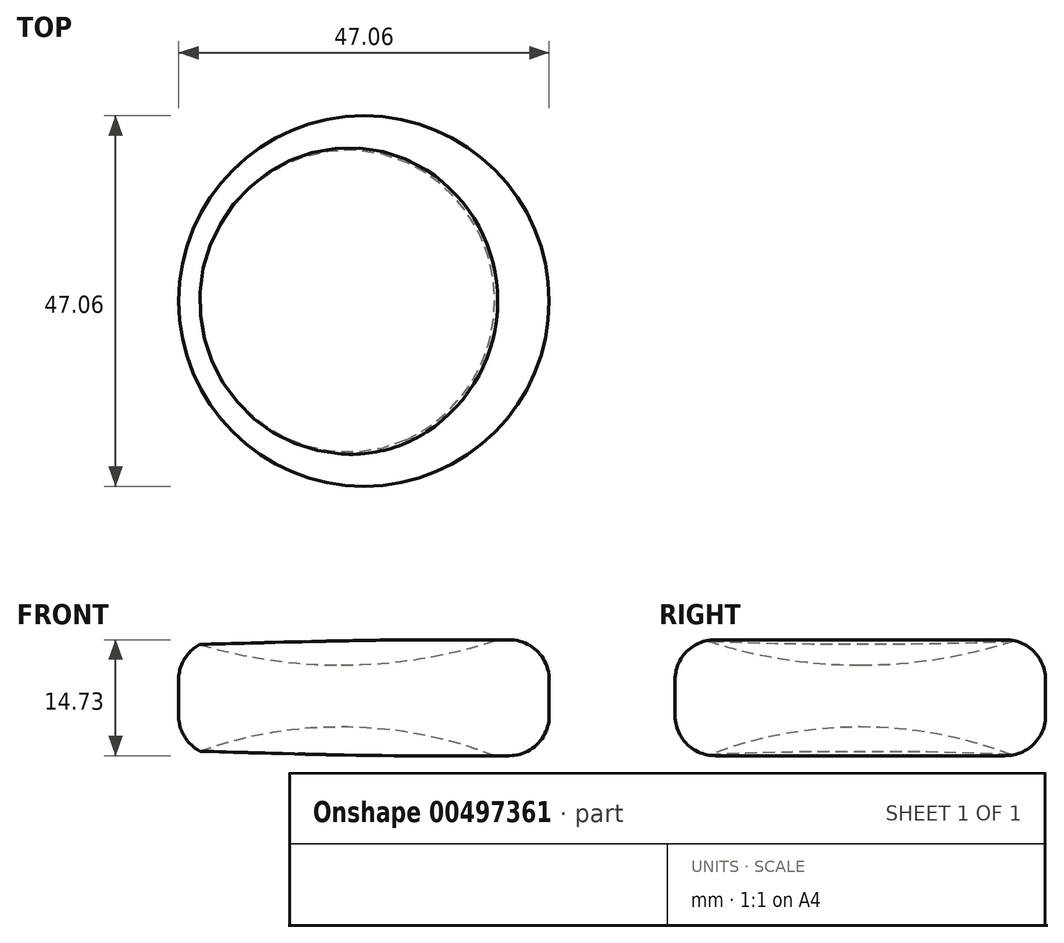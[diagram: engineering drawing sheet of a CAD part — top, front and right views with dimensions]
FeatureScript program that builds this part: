
annotation { "Feature Type Name" : "Feature", "Feature Type Description" : "" }
export const myFeature = defineFeature(function(context is Context, id is Id, definition is map)
    precondition{}
    {
        {
            var Q0;
            Q0=qCreatedBy(makeId("Top.planeOp"),FACE);
            var sketch = newSketch(context, id + "F0", { "sketchPlane" : qUnion([Q0])});
            skCircle(sketch, "E0", {"center": v(2.88, 0) * mm, "radius": 23.53 * mm});
            skSolve(sketch);
        }
        {
            var Q0;
            Q0=makeQuery(id+"F0.imprint","IMPRINT",FACE,{"disambiguationData":[TD([[makeQuery(id+"F0.imprint","IMPRINT",EDGE,{"derivedFrom":sQuery(id+"F0.wireOp",EDGE,"E0")}),1.0]])]});
            extrude(context, id + "F1", {"entities" : qUnion([Q0]), "depth" : 14.73 * mm});
        }
        {
            var Q0;
            Q0=makeQuery(id+"F1.opExtrude","SWEPT_FACE",FACE,{"disambiguationData":[OSD([sQuery(id+"F0.wireOp",EDGE,"E0")])]});
            fillet(context, id + "F2", {"entities" : qUnion([Q0]), "radius" : 5.08 * mm, "tangentPropagation" : true, "allowEdgeOverflow" : false});
        }
        {
            var Q0;
            Q0=qCreatedBy(makeId("Right.planeOp"),FACE);
            var sketch = newSketch(context, id + "F3", { "sketchPlane" : qUnion([Q0])});
            skCircle(sketch, "E1", {"center": v(0, -50.28) * mm, "radius": 53.92 * mm});
            skLineSegment(sketch, "E2", {"start": v(0, -50.28) * mm, "end": v(-53.92, -50.28) * mm});
            skLineSegment(sketch, "E3", {"start": v(-53.92, -50.28) * mm, "end": v(53.92, -50.28) * mm});
            skSolve(sketch);
        }
        {
            var Q0;
            {var subQ0=sQuery(id+"F3.wireOp",EDGE,"E3");var subQ4=makeQuery(id+"F3.imprint","IMPRINT",VERTEX,{"derivedFrom":subQ0});Q0=makeQuery(id+"F3.imprint","IMPRINT",FACE,{"disambiguationData":[TD([[makeQuery(id+"F3.imprint","IMPRINT",EDGE,{"disambiguationData":[TD([[subQ4,1.0]])],"derivedFrom":subQ0}),1.0]])]});}
            var Q1;
            Q1=sQuery(id+"F3.wireOp",EDGE,"E3");
            revolve(context, id + "F4", {"operationType" : NewBodyOperationType.REMOVE, "entities" : qUnion([Q0]), "axis" : qUnion([Q1]), "revolveType" : RevolveType.FULL, "oppositeDirection" : true});
        }
        {
            var Q0;
            Q0=qCreatedBy(makeId("Front.planeOp"),FACE);
            var sketch = newSketch(context, id + "F5", { "sketchPlane" : qUnion([Q0])});
            skCircle(sketch, "E4", {"center": v(0, -75.78) * mm, "radius": 78.03 * mm});
            skLineSegment(sketch, "E5", {"start": v(0, -162.58) * mm, "end": v(0, 39.57) * mm});
            skSolve(sketch);
        }
        {
            var Q0;
            {var subQ0=sQuery(id+"F5.wireOp",EDGE,"E5");var subQ1=sQuery(id+"F5.wireOp",EDGE,"E4");var subQ2=makeQuery(id+"F5.imprint","INTERSECT",VERTEX,{"disambiguationData":[OD(0.0)],"derivedFrom":[subQ1,subQ0]});Q0=makeQuery(id+"F5.imprint","IMPRINT",FACE,{"disambiguationData":[TD([[makeQuery(id+"F5.imprint","IMPRINT",EDGE,{"disambiguationData":[TD([[subQ2,1.0]])],"derivedFrom":subQ1}),1.0]])]});}
            var Q1;
            Q1=sQuery(id+"F5.wireOp",EDGE,"E5");
            revolve(context, id + "F6", {"operationType" : NewBodyOperationType.REMOVE, "entities" : qUnion([Q0]), "axis" : qUnion([Q1]), "revolveType" : RevolveType.FULL, "oppositeDirection" : true});
        }
        {
            var Q0;
            Q0=qCreatedBy(makeId("Right.planeOp"),FACE);
            var sketch = newSketch(context, id + "F7", { "sketchPlane" : qUnion([Q0])});
            skCircle(sketch, "E6", {"center": v(0, 74.51) * mm, "radius": 63 * mm});
            skLineSegment(sketch, "E7", {"start": v(0, 146.97) * mm, "end": v(0, -26.7) * mm});
            skSolve(sketch);
        }
        {
            var Q0;
            {var subQ0=sQuery(id+"F7.wireOp",EDGE,"E7");var subQ1=sQuery(id+"F7.wireOp",EDGE,"E6");var subQ2=makeQuery(id+"F7.imprint","INTERSECT",VERTEX,{"disambiguationData":[OD(0.0)],"derivedFrom":[subQ1,subQ0]});Q0=makeQuery(id+"F7.imprint","IMPRINT",FACE,{"disambiguationData":[TD([[makeQuery(id+"F7.imprint","IMPRINT",EDGE,{"disambiguationData":[TD([[subQ2,-1.0]])],"derivedFrom":subQ1}),1.0]])]});}
            var Q1;
            Q1=sQuery(id+"F7.wireOp",EDGE,"E7");
            revolve(context, id + "F8", {"operationType" : NewBodyOperationType.REMOVE, "entities" : qUnion([Q0]), "axis" : qUnion([Q1]), "revolveType" : RevolveType.FULL, "oppositeDirection" : true});
        }
    });
